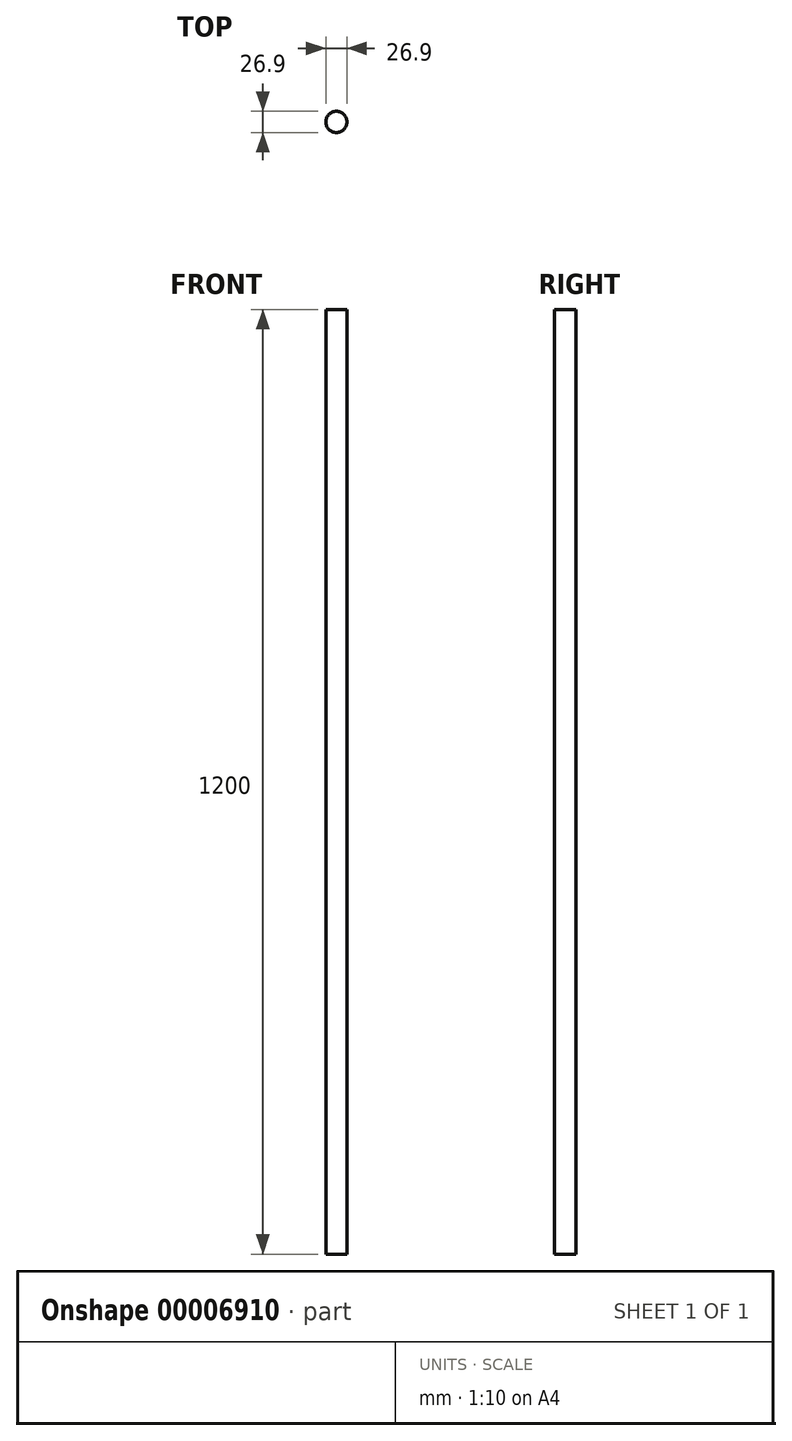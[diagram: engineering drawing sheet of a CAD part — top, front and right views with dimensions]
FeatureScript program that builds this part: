
annotation { "Feature Type Name" : "Feature", "Feature Type Description" : "" }
export const myFeature = defineFeature(function(context is Context, id is Id, definition is map)
    precondition{}
    {
        {
            var Q0;
            Q0=qCreatedBy(makeId("Top.planeOp"),FACE);
            var sketch = newSketch(context, id + "F0", { "sketchPlane" : qUnion([Q0])});
            skCircle(sketch, "E0", {"center": v(0, 0) * mm, "radius": 13.45 * mm});
            skSolve(sketch);
        }
        {
            var Q0;
            Q0=makeQuery(id+"F0.imprint","IMPRINT",FACE,{"disambiguationData":[TD([[makeQuery(id+"F0.imprint","IMPRINT",EDGE,{"derivedFrom":sQuery(id+"F0.wireOp",EDGE,"E0")}),1.0]])]});
            extrude(context, id + "F1", {"entities" : qUnion([Q0]), "depth" : (1200) * mm});
        }
    });
